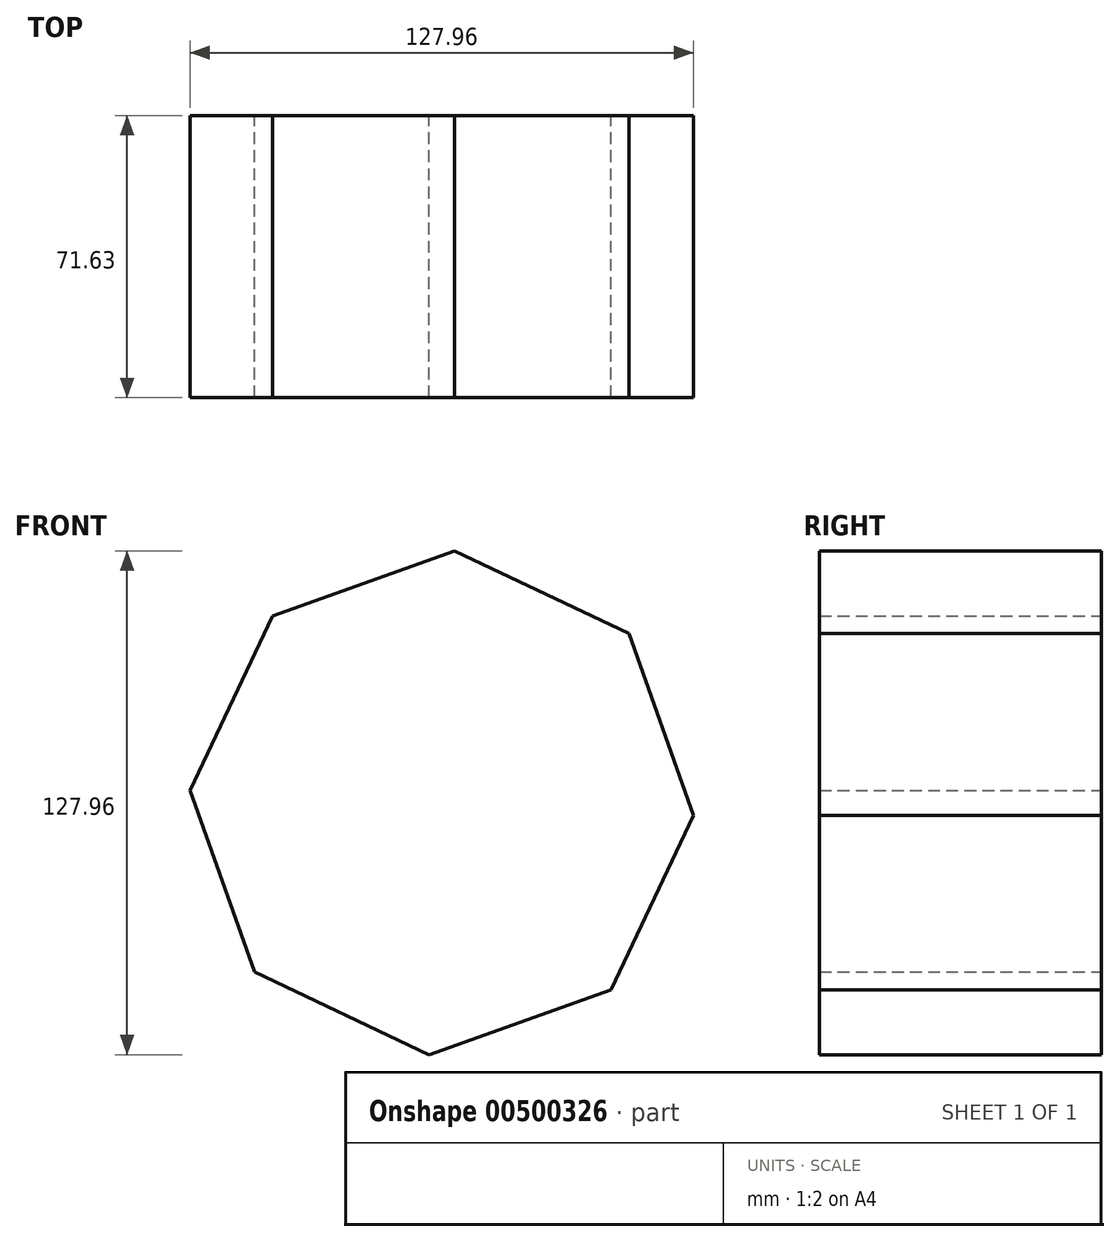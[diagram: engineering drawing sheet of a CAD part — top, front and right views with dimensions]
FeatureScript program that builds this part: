
annotation { "Feature Type Name" : "Feature", "Feature Type Description" : "" }
export const myFeature = defineFeature(function(context is Context, id is Id, definition is map)
    precondition{}
    {
        {
            var Q0;
            Q0=qCreatedBy(makeId("Front.planeOp"),FACE);
            var sketch = newSketch(context, id + "F0", { "sketchPlane" : qUnion([Q0])});
            skCircle(sketch, "E0.cCircle", {"center": v(0, 0) * mm, "radius": 64.06 * mm, "construction": true});
            skLineSegment(sketch, "E0.0", {"start": v(3.2, 63.98) * mm, "end": v(47.5, 42.97) * mm});
            skLineSegment(sketch, "E0.1", {"start": v(47.5, 42.97) * mm, "end": v(63.98, -3.2) * mm});
            skLineSegment(sketch, "E0.2", {"start": v(63.98, -3.2) * mm, "end": v(42.97, -47.5) * mm});
            skLineSegment(sketch, "E0.3", {"start": v(42.97, -47.5) * mm, "end": v(-3.2, -63.98) * mm});
            skLineSegment(sketch, "E0.4", {"start": v(-3.2, -63.98) * mm, "end": v(-47.5, -42.97) * mm});
            skLineSegment(sketch, "E0.5", {"start": v(-47.5, -42.97) * mm, "end": v(-63.98, 3.2) * mm});
            skLineSegment(sketch, "E0.6", {"start": v(-63.98, 3.2) * mm, "end": v(-42.97, 47.5) * mm});
            skLineSegment(sketch, "E0.7", {"start": v(-42.97, 47.5) * mm, "end": v(3.2, 63.98) * mm});
            skSolve(sketch);
        }
        {
            var Q0;
            Q0 = qSketchRegion(id + "F0", true);
            extrude(context, id + "F1", {"entities" : qUnion([Q0]), "depth" : 71.63 * mm});
        }
    });
